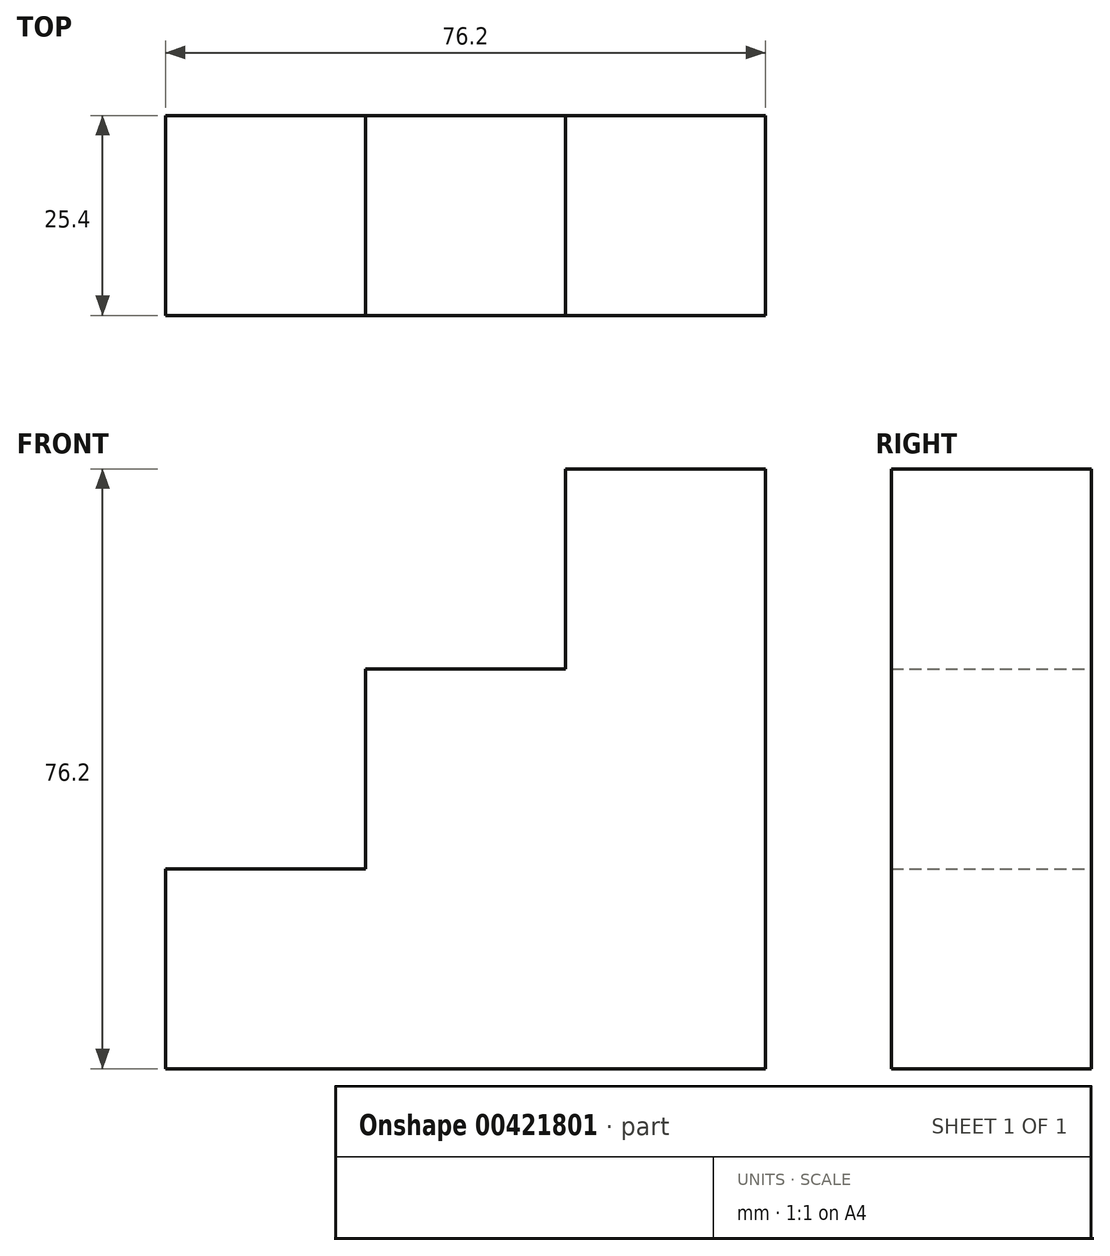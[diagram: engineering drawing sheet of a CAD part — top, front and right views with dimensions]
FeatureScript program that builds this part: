
annotation { "Feature Type Name" : "Feature", "Feature Type Description" : "" }
export const myFeature = defineFeature(function(context is Context, id is Id, definition is map)
    precondition{}
    {
        {
            var Q0;
            Q0=qCreatedBy(makeId("Front.planeOp"),FACE);
            var sketch = newSketch(context, id + "F0", { "sketchPlane" : qUnion([Q0])});
            skLineSegment(sketch, "E0", {"start": v(0, 0) * mm, "end": v(-76.2, 0) * mm});
            skLineSegment(sketch, "E1", {"start": v(-76.2, 0) * mm, "end": v(-76.2, 25.4) * mm});
            skLineSegment(sketch, "E2", {"start": v(-76.2, 25.4) * mm, "end": v(-50.8, 25.4) * mm});
            skLineSegment(sketch, "E3", {"start": v(-50.8, 25.4) * mm, "end": v(-50.8, 50.8) * mm});
            skLineSegment(sketch, "E4", {"start": v(-50.8, 50.8) * mm, "end": v(-25.4, 50.8) * mm});
            skLineSegment(sketch, "E5", {"start": v(-25.4, 50.8) * mm, "end": v(-25.4, 76.2) * mm});
            skLineSegment(sketch, "E6", {"start": v(-25.4, 76.2) * mm, "end": v(0, 76.2) * mm});
            skLineSegment(sketch, "E7", {"start": v(0, 76.2) * mm, "end": v(0, 0) * mm});
            skSolve(sketch);
        }
        {
            var Q0;
            Q0 = qSketchRegion(id + "F0", true);
            extrude(context, id + "F1", {"entities" : qUnion([Q0]), "depth" : 25.4 * mm});
        }
    });
